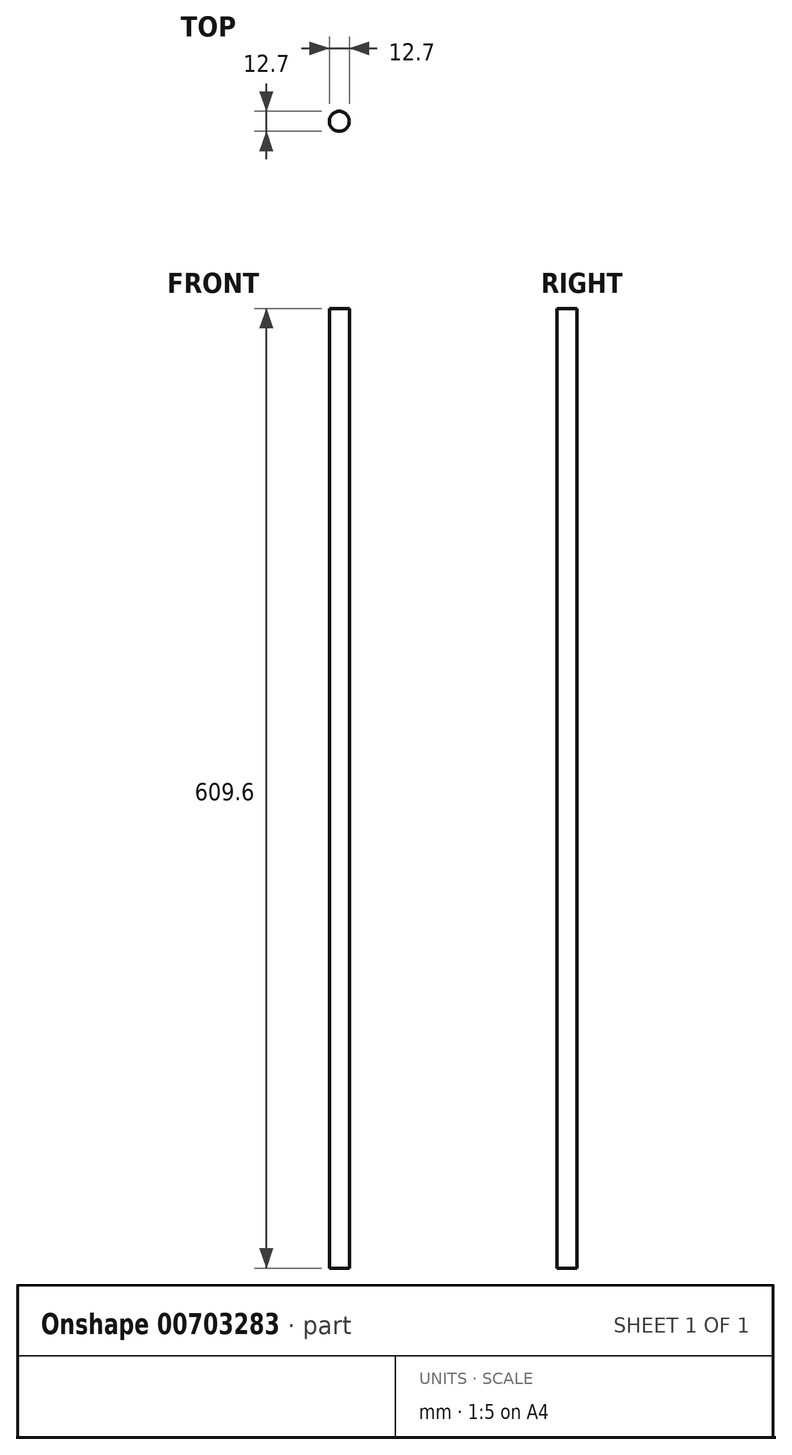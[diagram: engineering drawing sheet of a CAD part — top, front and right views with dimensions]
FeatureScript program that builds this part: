
annotation { "Feature Type Name" : "Feature", "Feature Type Description" : "" }
export const myFeature = defineFeature(function(context is Context, id is Id, definition is map)
    precondition{}
    {
        {
            var Q0;
            Q0=qCreatedBy(makeId("Top.planeOp"),FACE);
            var sketch = newSketch(context, id + "F0", { "sketchPlane" : qUnion([Q0])});
            skCircle(sketch, "E0", {"center": v(-90.6, -25.5) * mm, "radius": 6.35 * mm});
            skSolve(sketch);
        }
        {
            var Q0;
            Q0=makeQuery(id+"F0.imprint","IMPRINT",FACE,{"disambiguationData":[TD([[makeQuery(id+"F0.imprint","IMPRINT",EDGE,{"derivedFrom":sQuery(id+"F0.wireOp",EDGE,"E0")}),1.0]])]});
            extrude(context, id + "F1", {"entities" : qUnion([Q0]), "depth" : 609.6 * mm, "offsetDistance" : 25.4 * mm});
        }
    });
